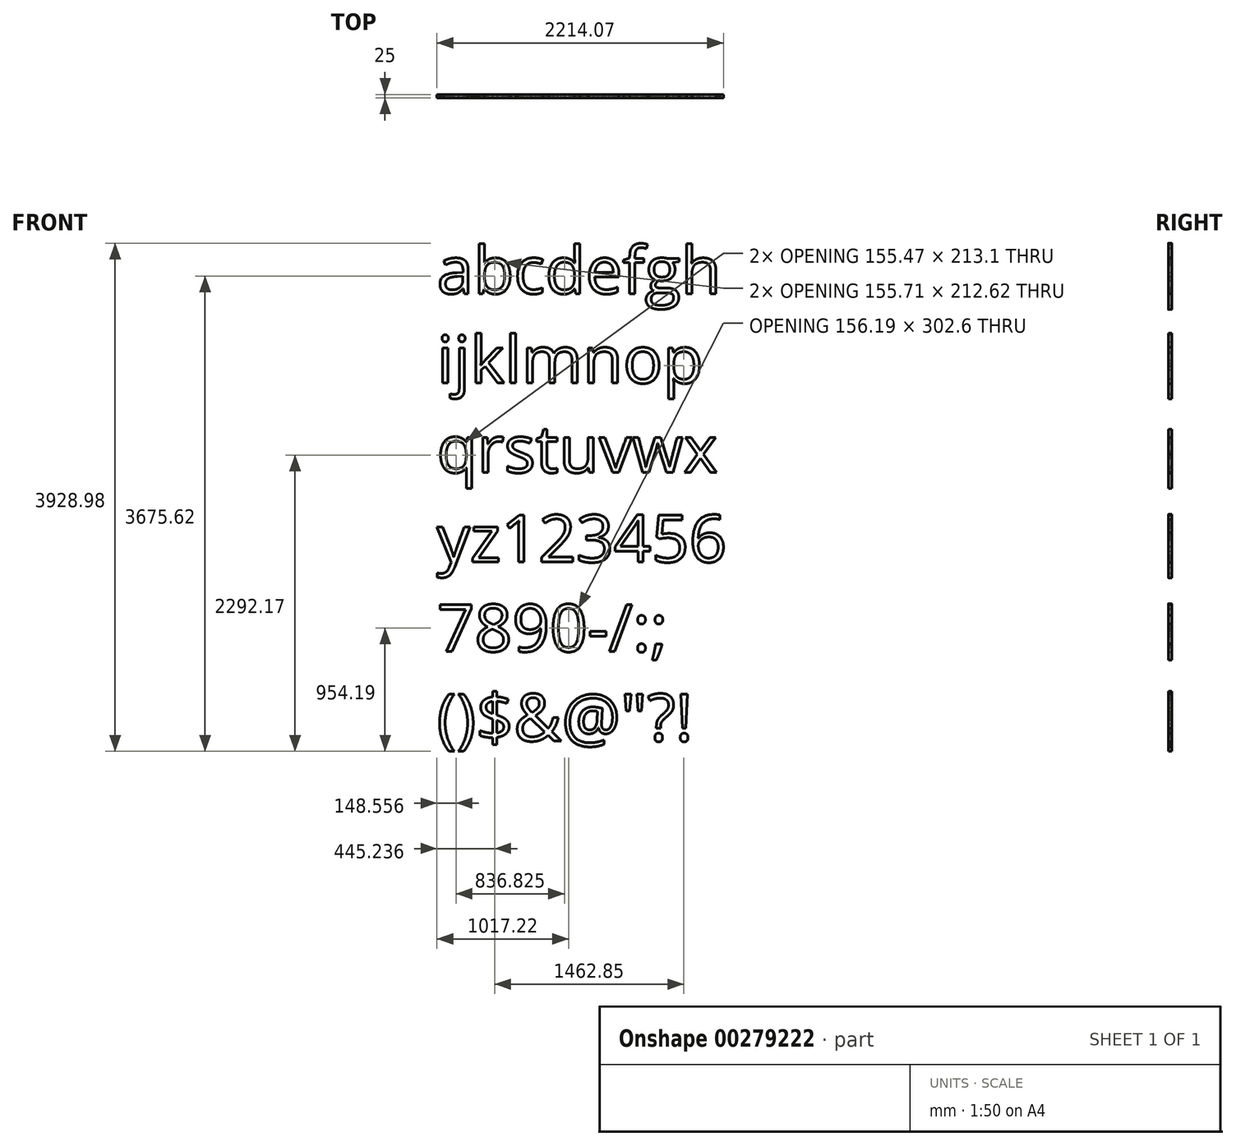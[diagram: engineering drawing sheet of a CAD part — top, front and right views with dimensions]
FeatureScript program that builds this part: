
annotation { "Feature Type Name" : "Feature", "Feature Type Description" : "" }
export const myFeature = defineFeature(function(context is Context, id is Id, definition is map)
    precondition{}
    {
        {
            var Q0;
            Q0=qCreatedBy(makeId("Front.planeOp"),FACE);
            var sketch = newSketch(context, id + "F0", { "sketchPlane" : qUnion([Q0])});
            skText(sketch, "E0", { "text": "abcdefgh\nijklmnop\nqrstuvwx\nyz123456\n7890-/:;\n()$&@\"?!", "fontName": "OpenSans-Regular.ttf"});
            const initialGuessF0  = {"E0": [-0.14609, -0.17382, 1, 0, 0.36627]};
            skSetInitialGuess(sketch, initialGuessF0);
            skSolve(sketch);
        }
        {
            var Q0;
            Q0 = qSketchRegion(id + "F0", true);
            extrude(context, id + "F1", {"entities" : qUnion([Q0]), "depth" : 25 * mm});
        }
    });
